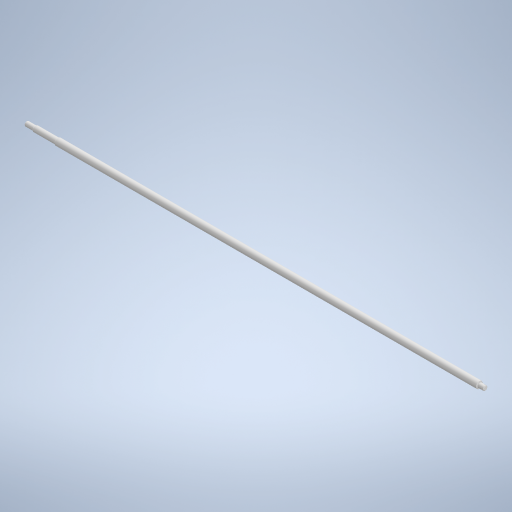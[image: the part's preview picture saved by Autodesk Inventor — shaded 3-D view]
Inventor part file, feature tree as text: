
AUTODESK INVENTOR PART (.ipt)
format: ipt  version: 2023 (Build 270158000, 158)  size: 267,264 bytes
history: native  units: in
note: dims shown in document units (in); Inventor stores cm internally (conversion verified against a paired STEP export)
features: revolve x1, sketch x1
ambient origin geometry x8: Origin, YZ Plane, XZ Plane, XY Plane, X Axis, Y Axis, Z Axis, Center Point
bodies: Solid1 (feature_tree)
feature tree (2):
  revolve  "Revolution1"  [1 undecoded]
  sketch  "Sketch1"  dims[d0=0.1575in d1=0.1969in d2=0.2362in d3=135.0deg d4=135.0deg d5=0.5906in d6=1.5354in d7=135.0deg d8=0.1575in d9=0.2756in d10=0.3937in d11=0.0079in d12=0.0354in d14=135.0deg d15=31.4961in d16=90.0deg]
note: 1 required parameter value undecoded (feature->parameter linkage not recoverable at this tier; creation-order binding heuristic only, values carry confidence <= 0.55)
